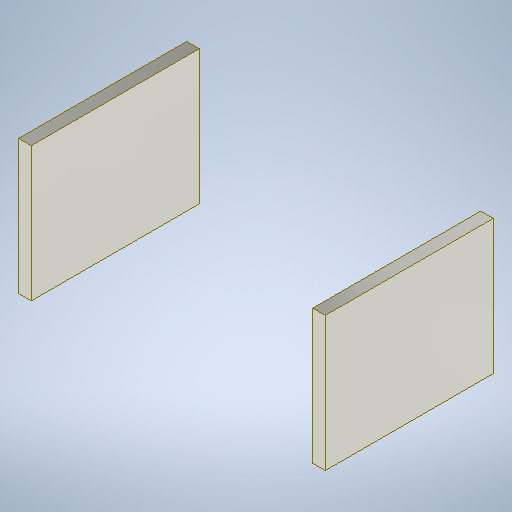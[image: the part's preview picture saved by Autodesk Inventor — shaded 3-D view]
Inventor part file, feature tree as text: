
AUTODESK INVENTOR PART (.ipt)
format: ipt  version: 2025.1 (Build 291241000, 241)  size: 223,232 bytes
history: native  units: mm
features: extrude x1, sketch x1
ambient origin geometry x8: Origin, YZ Plane, XZ Plane, XY Plane, X Axis, Y Axis, Z Axis, Center Point
bodies: Solid1 (feature_tree)
feature tree (2):
  extrude  "Extrusion1"  Depth=3.0mm
  sketch  "Sketch1"  dims[d0=73.0mm d1=3.0mm d2=32.0mm d3=16.0mm d5=0.0mm]
